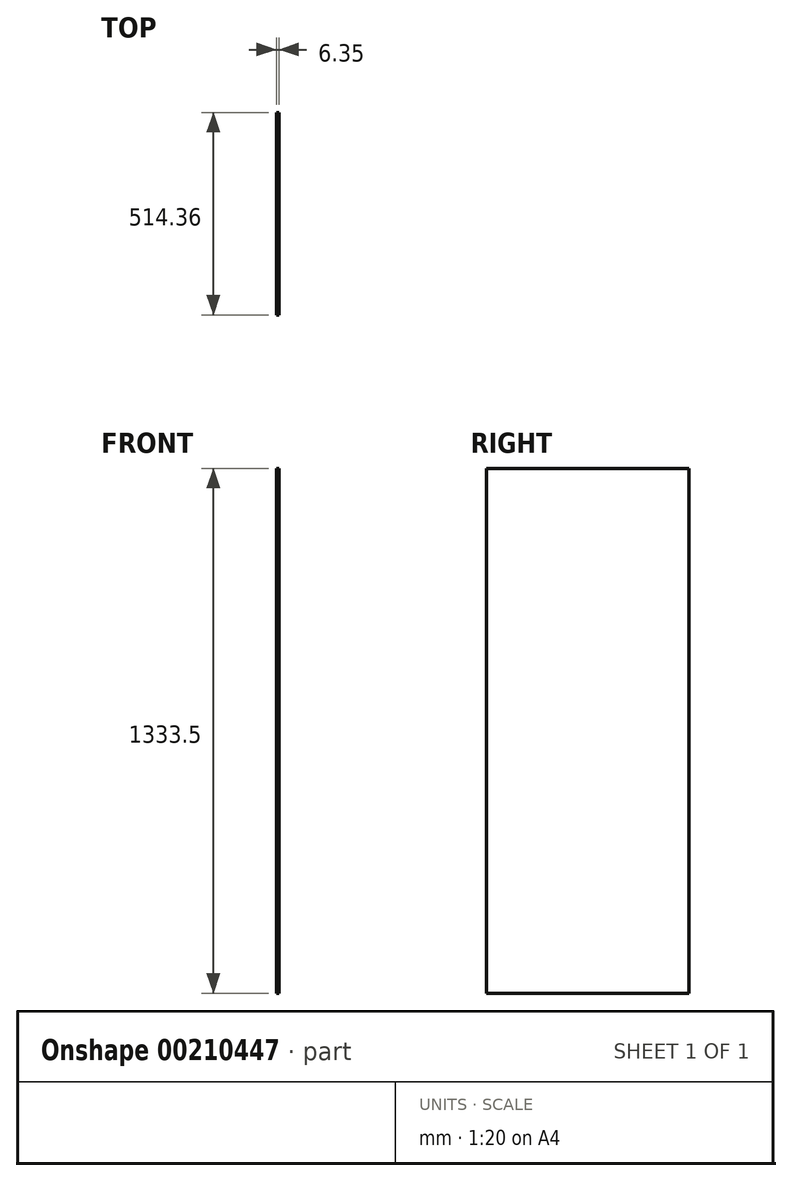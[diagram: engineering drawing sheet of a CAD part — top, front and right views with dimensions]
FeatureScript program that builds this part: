
annotation { "Feature Type Name" : "Feature", "Feature Type Description" : "" }
export const myFeature = defineFeature(function(context is Context, id is Id, definition is map)
    precondition{}
    {
        {
            var Q0;
            Q0=qCreatedBy(makeId("Right.planeOp"),FACE);
            var sketch = newSketch(context, id + "F0", { "sketchPlane" : qUnion([Q0])});
            skLineSegment(sketch, "E0.bottom", {"start": v(257.18, 666.75) * mm, "end": v(-257.18, 666.75) * mm});
            skLineSegment(sketch, "E0.top", {"start": v(257.18, -666.75) * mm, "end": v(-257.18, -666.75) * mm});
            skLineSegment(sketch, "E0.left", {"start": v(257.18, 666.75) * mm, "end": v(257.18, -666.75) * mm});
            skLineSegment(sketch, "E0.right", {"start": v(-257.18, 666.75) * mm, "end": v(-257.18, -666.75) * mm});
            skPoint(sketch, "E0.middle", {"position": v(0, 0) * mm});
            skSolve(sketch);
        }
        {
            var Q0;
            Q0=makeQuery(id+"F0.imprint","IMPRINT",FACE,{"disambiguationData":[TD([[makeQuery(id+"F0.imprint","IMPRINT",EDGE,{"derivedFrom":sQuery(id+"F0.wireOp",EDGE,"E0.bottom")}),1.0]])]});
            extrude(context, id + "F1", {"entities" : qUnion([Q0]), "depth" : 6.35 * mm});
        }
    });
